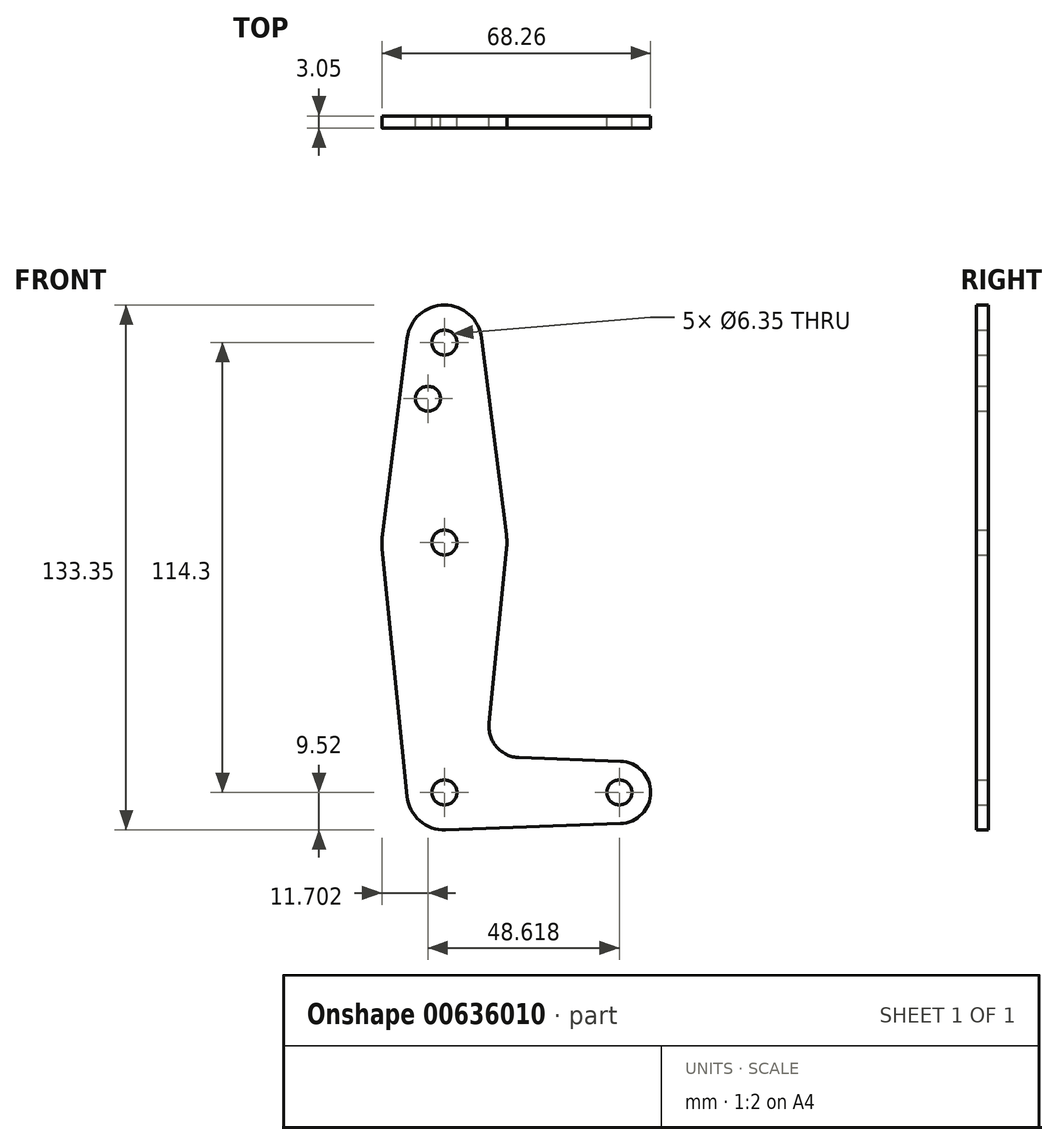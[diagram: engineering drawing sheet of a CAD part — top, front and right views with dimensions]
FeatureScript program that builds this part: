
annotation { "Feature Type Name" : "Feature", "Feature Type Description" : "" }
export const myFeature = defineFeature(function(context is Context, id is Id, definition is map)
    precondition{}
    {
        {
            var Q0;
            Q0=qCreatedBy(makeId("Front.planeOp"),FACE);
            var sketch = newSketch(context, id + "F0", { "sketchPlane" : qUnion([Q0])});
            skLineSegment(sketch, "E0", {"start": v(0, 0) * mm, "end": v(0, 114.3) * mm, "construction": true});
            skLineSegment(sketch, "E1", {"start": v(0, 0) * mm, "end": v(44.45, 0) * mm, "construction": true});
            skCircle(sketch, "E2", {"center": v(0, 114.3) * mm, "radius": 9.53 * mm});
            skCircle(sketch, "E3", {"center": v(0, 63.5) * mm, "radius": 15.88 * mm});
            skCircle(sketch, "E4", {"center": v(0, 0) * mm, "radius": 9.53 * mm});
            skCircle(sketch, "E5", {"center": v(44.45, 0) * mm, "radius": 7.94 * mm});
            skCircle(sketch, "E6", {"center": v(0, 114.3) * mm, "radius": 3.17 * mm});
            skCircle(sketch, "E7", {"center": v(0, 63.5) * mm, "radius": 3.18 * mm});
            skCircle(sketch, "E8", {"center": v(0, 0) * mm, "radius": 3.18 * mm});
            skCircle(sketch, "E9", {"center": v(44.45, 0) * mm, "radius": 3.18 * mm});
            skCircle(sketch, "E10", {"center": v(-4.17, 100.03) * mm, "radius": 3.18 * mm});
            skLineSegment(sketch, "E11", {"start": v(-9.45, 115.5) * mm, "end": v(-15.75, 65.48) * mm});
            skLineSegment(sketch, "E12", {"start": v(9.45, 115.5) * mm, "end": v(15.75, 65.48) * mm});
            skLineSegment(sketch, "E13", {"start": v(44.73, -7.93) * mm, "end": v(0, -9.53) * mm});
            skLineSegment(sketch, "E14", {"start": v(15.8, 61.91) * mm, "end": v(11.34, 17.6) * mm});
            skLineSegment(sketch, "E15", {"start": v(18.97, 8.85) * mm, "end": v(44.73, 7.93) * mm});
            skArc(sketch, "E16.filletArc", {"start": v(11.34, 17.6) * mm, "mid": v(13.26, 11.57) * mm, "end": v(18.97, 8.85) * mm});
            skLineSegment(sketch, "E17", {"start": v(-15.8, 61.91) * mm, "end": v(-9.48, -0.95) * mm});
            skSolve(sketch);
        }
        {
            var Q0;
            Q0 = qSketchRegion(id + "F0", true);
            extrude(context, id + "F1", {"entities" : qUnion([Q0]), "depth" : 3.05 * mm, "offsetDistance" : 25.4 * mm});
        }
    });
